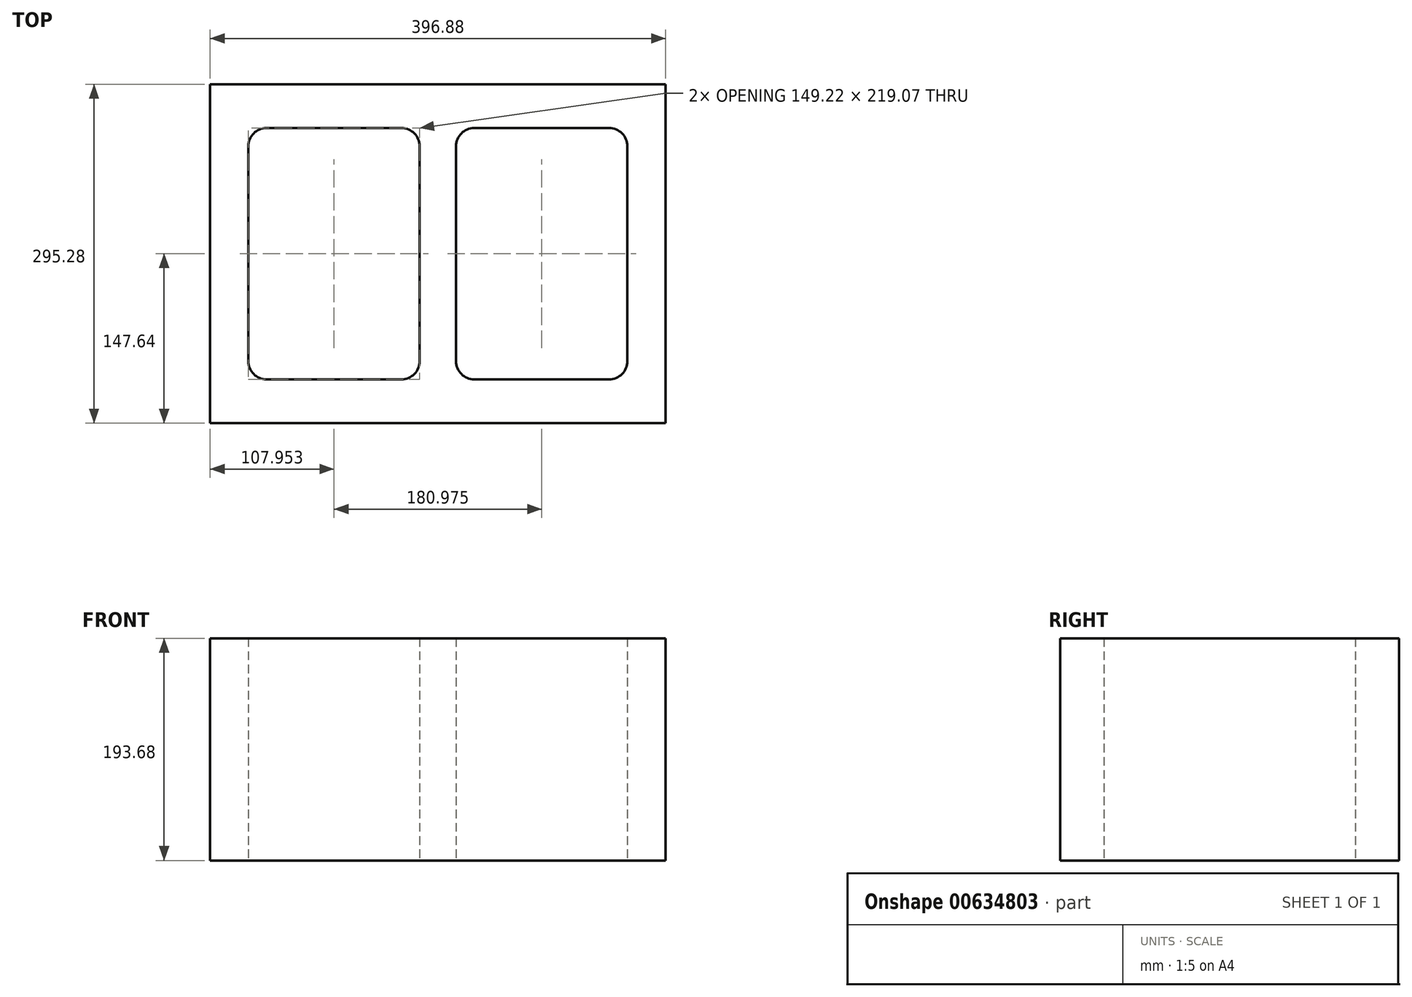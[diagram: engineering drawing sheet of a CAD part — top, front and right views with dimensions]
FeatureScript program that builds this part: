
annotation { "Feature Type Name" : "Feature", "Feature Type Description" : "" }
export const myFeature = defineFeature(function(context is Context, id is Id, definition is map)
    precondition{}
    {
        {
            var Q0;
            Q0=qCreatedBy(makeId("Top.planeOp"),FACE);
            var sketch = newSketch(context, id + "F0", { "sketchPlane" : qUnion([Q0])});
            skLineSegment(sketch, "E0.bottom", {"start": v(-198.44, 147.64) * mm, "end": v(198.44, 147.64) * mm});
            skLineSegment(sketch, "E0.top", {"start": v(-198.44, -147.64) * mm, "end": v(198.44, -147.64) * mm});
            skLineSegment(sketch, "E0.left", {"start": v(-198.44, 147.64) * mm, "end": v(-198.44, -147.64) * mm});
            skLineSegment(sketch, "E0.right", {"start": v(198.44, 147.64) * mm, "end": v(198.44, -147.64) * mm});
            skLineSegment(sketch, "E1.bottom", {"start": v(-149.22, 109.54) * mm, "end": v(-31.75, 109.54) * mm});
            skLineSegment(sketch, "E1.top", {"start": v(-149.22, -109.54) * mm, "end": v(-31.75, -109.54) * mm});
            skLineSegment(sketch, "E1.left", {"start": v(-165.1, 93.66) * mm, "end": v(-165.1, -93.66) * mm});
            skLineSegment(sketch, "E1.right", {"start": v(-15.87, 93.66) * mm, "end": v(-15.88, -93.66) * mm});
            skLineSegment(sketch, "E2", {"start": v(0, 147.64) * mm, "end": v(0, -147.64) * mm, "construction": true});
            skLineSegment(sketch, "E3.MirrorCS", {"start": v(165.1, 93.66) * mm, "end": v(165.1, -93.66) * mm});
            skLineSegment(sketch, "E4.MirrorCS", {"start": v(149.22, 109.54) * mm, "end": v(31.75, 109.54) * mm});
            skLineSegment(sketch, "E5.MirrorCS", {"start": v(149.22, -109.54) * mm, "end": v(31.75, -109.54) * mm});
            skLineSegment(sketch, "E6.MirrorCS", {"start": v(15.87, 93.66) * mm, "end": v(15.88, -93.66) * mm});
            skLineSegment(sketch, "E7", {"start": v(-15.87, 0) * mm, "end": v(15.87, 0) * mm});
            skPoint(sketch, "E8.visualSharp", {"position": v(-165.1, 109.54) * mm});
            skArc(sketch, "E8.filletArc", {"start": v(-149.22, 109.54) * mm, "mid": v(-160.45, 104.89) * mm, "end": v(-165.1, 93.66) * mm});
            skPoint(sketch, "E9.visualSharp", {"position": v(-165.1, -109.54) * mm});
            skArc(sketch, "E9.filletArc", {"start": v(-165.1, -93.66) * mm, "mid": v(-160.45, -104.89) * mm, "end": v(-149.22, -109.54) * mm});
            skPoint(sketch, "E10.visualSharp", {"position": v(-15.88, -109.54) * mm});
            skArc(sketch, "E10.filletArc", {"start": v(-31.75, -109.54) * mm, "mid": v(-20.52, -104.89) * mm, "end": v(-15.87, -93.66) * mm});
            skPoint(sketch, "E11.visualSharp", {"position": v(-15.88, 109.54) * mm});
            skArc(sketch, "E11.filletArc", {"start": v(-15.88, 93.66) * mm, "mid": v(-20.52, 104.89) * mm, "end": v(-31.75, 109.54) * mm});
            skPoint(sketch, "E12.visualSharp", {"position": v(15.87, 109.54) * mm});
            skArc(sketch, "E12.filletArc", {"start": v(31.75, 109.54) * mm, "mid": v(20.52, 104.89) * mm, "end": v(15.88, 93.66) * mm});
            skPoint(sketch, "E13.visualSharp", {"position": v(165.1, -109.54) * mm});
            skArc(sketch, "E13.filletArc", {"start": v(149.22, -109.54) * mm, "mid": v(160.45, -104.89) * mm, "end": v(165.1, -93.66) * mm});
            skPoint(sketch, "E14.visualSharp", {"position": v(165.1, 109.54) * mm});
            skArc(sketch, "E14.filletArc", {"start": v(165.1, 93.66) * mm, "mid": v(160.45, 104.89) * mm, "end": v(149.22, 109.54) * mm});
            skPoint(sketch, "E15.visualSharp", {"position": v(15.88, -109.54) * mm});
            skArc(sketch, "E15.filletArc", {"start": v(15.88, -93.66) * mm, "mid": v(20.52, -104.89) * mm, "end": v(31.75, -109.54) * mm});
            skSolve(sketch);
        }
        {
            var Q0;
            Q0=makeQuery(id+"F0.imprint","IMPRINT",FACE,{"disambiguationData":[TD([[makeQuery(id+"F0.imprint","IMPRINT",EDGE,{"derivedFrom":sQuery(id+"F0.wireOp",EDGE,"E0.bottom")}),-1.0]])]});
            extrude(context, id + "F1", {"entities" : qUnion([Q0]), "endBound" : BoundingType.SYMMETRIC, "depth" : 193.67 * mm, "offsetDistance" : 25.4 * mm});
        }
    });
